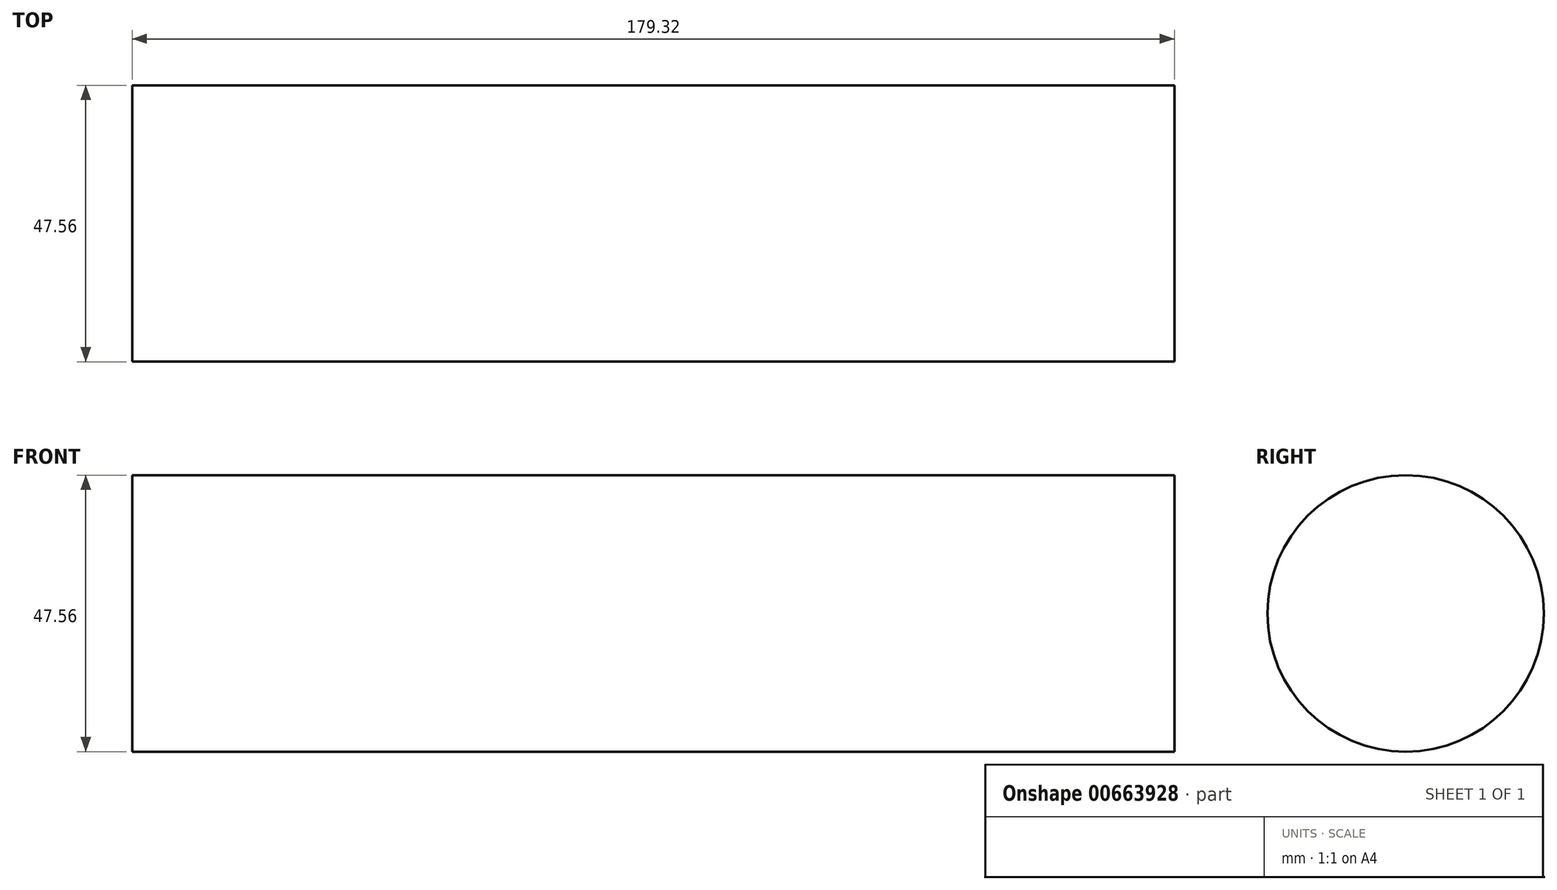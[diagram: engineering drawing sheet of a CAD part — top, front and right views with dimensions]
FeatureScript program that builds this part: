
annotation { "Feature Type Name" : "Feature", "Feature Type Description" : "" }
export const myFeature = defineFeature(function(context is Context, id is Id, definition is map)
    precondition{}
    {
        {
            var Q0;
            Q0=qCreatedBy(makeId("Right.planeOp"),FACE);
            var sketch = newSketch(context, id + "F0", { "sketchPlane" : qUnion([Q0])});
            skCircle(sketch, "E0", {"center": v(-98.37, 61.06) * mm, "radius": 23.78 * mm});
            skSolve(sketch);
        }
        {
            var Q0;
            Q0 = qSketchRegion(id + "F0", true);
            extrude(context, id + "F1", {"entities" : qUnion([Q0]), "depth" : 179.32 * mm, "offsetDistance" : 25.4 * mm});
        }
    });
